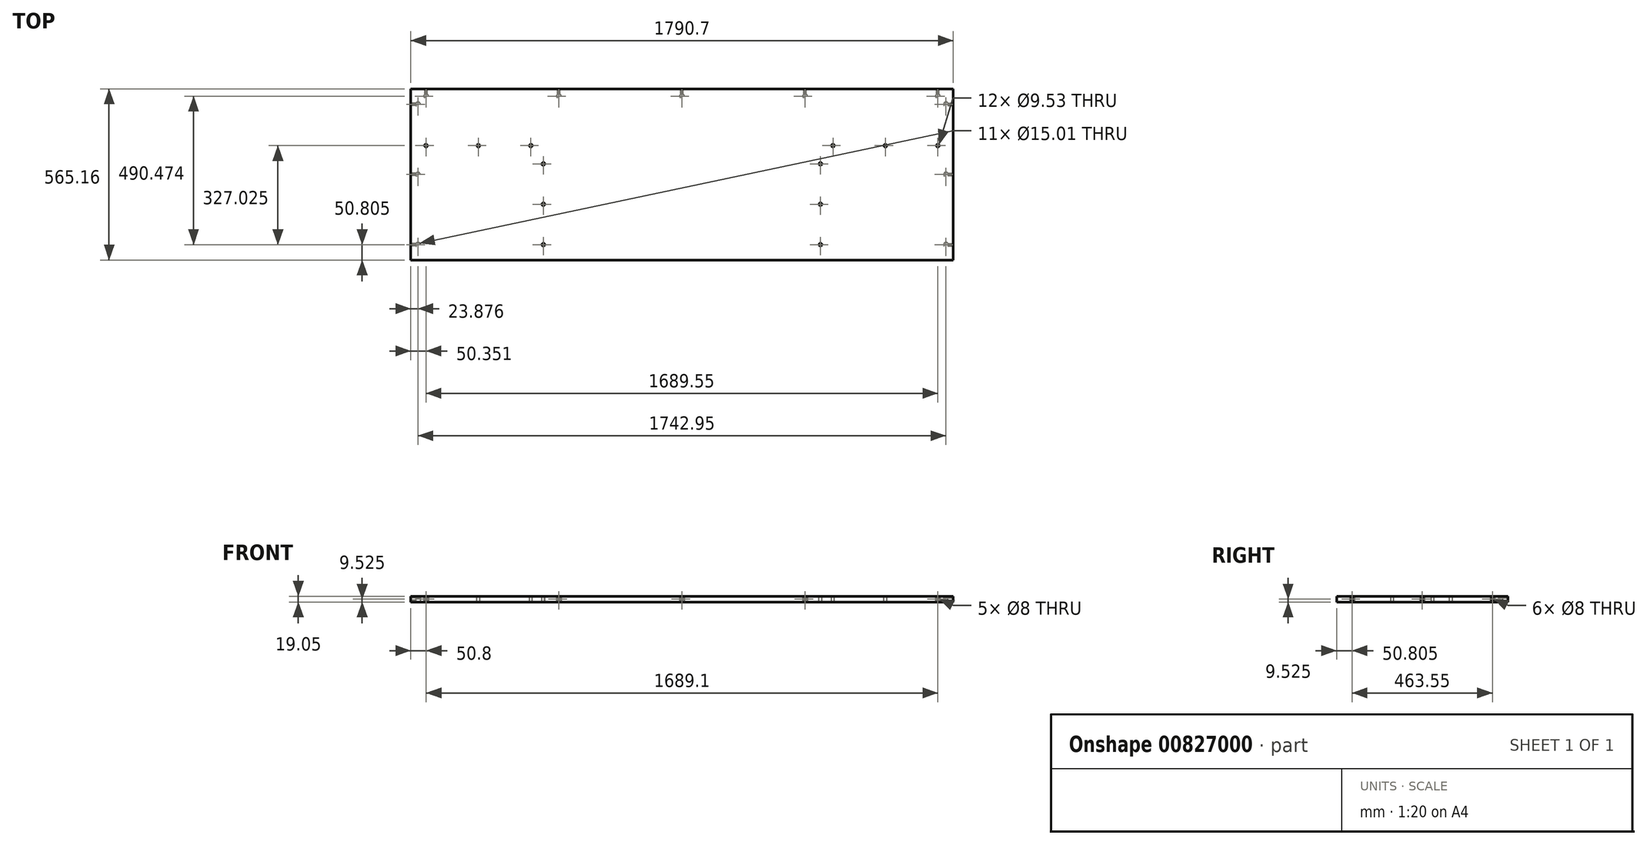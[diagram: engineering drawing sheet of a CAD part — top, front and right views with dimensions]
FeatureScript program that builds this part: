
annotation { "Feature Type Name" : "Feature", "Feature Type Description" : "" }
export const myFeature = defineFeature(function(context is Context, id is Id, definition is map)
    precondition{}
    {
        {
            var Q0;
            Q0=qCreatedBy(makeId("Top.planeOp"),FACE);
            var sketch = newSketch(context, id + "F0", { "sketchPlane" : qUnion([Q0])});
            skLineSegment(sketch, "E0.bottom", {"start": v(895.35, 282.58) * mm, "end": v(-895.35, 282.58) * mm});
            skLineSegment(sketch, "E0.top", {"start": v(895.35, -282.57) * mm, "end": v(-895.35, -282.57) * mm});
            skLineSegment(sketch, "E0.left", {"start": v(895.35, 282.58) * mm, "end": v(895.35, -282.57) * mm});
            skLineSegment(sketch, "E0.right", {"start": v(-895.35, 282.58) * mm, "end": v(-895.35, -282.57) * mm});
            skPoint(sketch, "E0.middle", {"position": v(0, 0) * mm});
            skSolve(sketch);
        }
        {
            var Q0;
            Q0=makeQuery(id+"F0.imprint","IMPRINT",FACE,{"disambiguationData":[TD([[makeQuery(id+"F0.imprint","IMPRINT",EDGE,{"derivedFrom":sQuery(id+"F0.wireOp",EDGE,"E0.bottom")}),1.0]])]});
            extrude(context, id + "F1", {"entities" : qUnion([Q0]), "depth" : 19.05 * mm, "offsetDistance" : 25.4 * mm});
        }
        {
            var Q0;
            Q0=makeQuery(id+"F1.opExtrude","CAP_FACE",FACE,{"disambiguationData":[OSD([sQuery(id+"F0.wireOp",EDGE,"E0.bottom"),sQuery(id+"F0.wireOp",EDGE,"E0.top"),sQuery(id+"F0.wireOp",EDGE,"E0.left"),sQuery(id+"F0.wireOp",EDGE,"E0.right")])],"isStart":false});
            var sketch = newSketch(context, id + "F2", { "sketchPlane" : qUnion([Q0])});
            skLineSegment(sketch, "E1.bottom", {"start": v(-895.35, 282.58) * mm, "end": v(-914.4, 282.58) * mm});
            skLineSegment(sketch, "E1.top", {"start": v(-895.35, -282.57) * mm, "end": v(-914.4, -282.57) * mm});
            skLineSegment(sketch, "E1.left", {"start": v(-895.35, 282.58) * mm, "end": v(-895.35, -282.57) * mm});
            skLineSegment(sketch, "E1.right", {"start": v(-914.4, 282.58) * mm, "end": v(-914.4, -282.57) * mm});
            skLineSegment(sketch, "E2.bottom", {"start": v(895.35, 282.58) * mm, "end": v(914.4, 282.58) * mm});
            skLineSegment(sketch, "E2.top", {"start": v(895.35, -282.57) * mm, "end": v(914.4, -282.57) * mm});
            skLineSegment(sketch, "E2.left", {"start": v(895.35, 282.58) * mm, "end": v(895.35, -282.57) * mm});
            skLineSegment(sketch, "E2.right", {"start": v(914.4, 282.58) * mm, "end": v(914.4, -282.57) * mm});
            skLineSegment(sketch, "E3", {"start": v(-914.4, -282.57) * mm, "end": v(-913.26, -282.57) * mm});
            skLineSegment(sketch, "E4.bottom", {"start": v(-913.26, -282.57) * mm, "end": v(-459.1, -282.57) * mm});
            skLineSegment(sketch, "E4.top", {"start": v(-913.26, -301.62) * mm, "end": v(-459.1, -301.62) * mm});
            skLineSegment(sketch, "E4.left", {"start": v(-913.26, -282.57) * mm, "end": v(-913.26, -301.62) * mm});
            skLineSegment(sketch, "E4.right", {"start": v(-459.1, -282.57) * mm, "end": v(-459.1, -301.62) * mm});
            skLineSegment(sketch, "E5", {"start": v(-459.1, -282.57) * mm, "end": v(-455.93, -282.57) * mm});
            skLineSegment(sketch, "E6.bottom", {"start": v(-455.93, -282.57) * mm, "end": v(-1.78, -282.57) * mm});
            skLineSegment(sketch, "E6.top", {"start": v(-455.93, -301.62) * mm, "end": v(-1.78, -301.62) * mm});
            skLineSegment(sketch, "E6.left", {"start": v(-455.93, -282.57) * mm, "end": v(-455.93, -301.62) * mm});
            skLineSegment(sketch, "E6.right", {"start": v(-1.78, -282.57) * mm, "end": v(-1.78, -301.62) * mm});
            skLineSegment(sketch, "E7", {"start": v(-1.78, -282.57) * mm, "end": v(1.4, -282.57) * mm});
            skLineSegment(sketch, "E8.bottom", {"start": v(1.4, -282.57) * mm, "end": v(455.55, -282.57) * mm});
            skLineSegment(sketch, "E8.top", {"start": v(1.4, -301.62) * mm, "end": v(455.55, -301.62) * mm});
            skLineSegment(sketch, "E8.left", {"start": v(1.4, -282.57) * mm, "end": v(1.4, -301.62) * mm});
            skLineSegment(sketch, "E8.right", {"start": v(455.55, -282.57) * mm, "end": v(455.55, -301.62) * mm});
            skLineSegment(sketch, "E9", {"start": v(455.55, -282.57) * mm, "end": v(458.72, -282.57) * mm});
            skLineSegment(sketch, "E10.bottom", {"start": v(458.72, -282.57) * mm, "end": v(912.88, -282.57) * mm});
            skLineSegment(sketch, "E10.top", {"start": v(458.72, -301.62) * mm, "end": v(912.88, -301.62) * mm});
            skLineSegment(sketch, "E10.left", {"start": v(458.72, -282.57) * mm, "end": v(458.72, -301.62) * mm});
            skLineSegment(sketch, "E10.right", {"start": v(912.88, -282.57) * mm, "end": v(912.88, -301.62) * mm});
            skLineSegment(sketch, "E11.left", {"start": v(-895.35, 282.58) * mm, "end": v(-895.8, 104.78) * mm});
            skLineSegment(sketch, "E11.right", {"start": v(895.8, 282.57) * mm, "end": v(895.35, 104.78) * mm});
            skLineSegment(sketch, "E12.left", {"start": v(-895.8, 104.78) * mm, "end": v(-895.8, 85.73) * mm});
            skLineSegment(sketch, "E12.right", {"start": v(895.35, 104.78) * mm, "end": v(895.35, 85.73) * mm});
            skLineSegment(sketch, "E13", {"start": v(-895.8, 95.25) * mm, "end": v(-845, 95.25) * mm});
            skLineSegment(sketch, "E14", {"start": v(895.35, 95.25) * mm, "end": v(844.55, 95.25) * mm});
            skLineSegment(sketch, "E15", {"start": v(-457.52, -282.57) * mm, "end": v(-457.68, 85.72) * mm});
            skLineSegment(sketch, "E16", {"start": v(457.14, -282.57) * mm, "end": v(457.14, 85.73) * mm});
            skLineSegment(sketch, "E17", {"start": v(-457.68, 85.72) * mm, "end": v(-457.66, 34.93) * mm});
            skLineSegment(sketch, "E18", {"start": v(-457.52, -282.57) * mm, "end": v(-457.54, -231.78) * mm});
            skLineSegment(sketch, "E19", {"start": v(457.14, -282.57) * mm, "end": v(457.14, -231.77) * mm});
            skLineSegment(sketch, "E20", {"start": v(457.14, 85.73) * mm, "end": v(457.14, 34.93) * mm});
            skPoint(sketch, "E21", {"position": v(-457.6, -98.43) * mm});
            skPoint(sketch, "E22", {"position": v(-457.66, 34.93) * mm});
            skPoint(sketch, "E23", {"position": v(-457.54, -231.78) * mm});
            skPoint(sketch, "E24", {"position": v(457.14, -231.77) * mm});
            skPoint(sketch, "E25", {"position": v(457.14, 34.93) * mm});
            skPoint(sketch, "E26", {"position": v(457.14, -98.42) * mm});
            skLineSegment(sketch, "E27.bottom", {"start": v(-448.07, 85.73) * mm, "end": v(-467.12, 85.73) * mm});
            skLineSegment(sketch, "E27.top", {"start": v(-448.07, -282.57) * mm, "end": v(-467.12, -282.57) * mm});
            skLineSegment(sketch, "E27.left", {"start": v(-448.07, 85.72) * mm, "end": v(-448.07, -282.58) * mm});
            skLineSegment(sketch, "E27.right", {"start": v(-467.12, 85.72) * mm, "end": v(-467.12, -282.58) * mm});
            skLineSegment(sketch, "E28.bottom", {"start": v(466.66, 85.73) * mm, "end": v(447.61, 85.73) * mm});
            skLineSegment(sketch, "E28.top", {"start": v(466.66, -282.57) * mm, "end": v(447.61, -282.57) * mm});
            skLineSegment(sketch, "E28.left", {"start": v(466.66, 85.73) * mm, "end": v(466.66, -282.57) * mm});
            skLineSegment(sketch, "E28.right", {"start": v(447.61, 85.73) * mm, "end": v(447.61, -282.57) * mm});
            skLineSegment(sketch, "E29.bottom", {"start": v(-448.07, 85.73) * mm, "end": v(-895.8, 85.73) * mm});
            skLineSegment(sketch, "E29.top", {"start": v(-448.07, 104.78) * mm, "end": v(-895.8, 104.78) * mm});
            skLineSegment(sketch, "E29.left", {"start": v(-448.07, 85.72) * mm, "end": v(-448.07, 104.78) * mm});
            skLineSegment(sketch, "E29.right", {"start": v(-895.8, 85.73) * mm, "end": v(-895.8, 104.78) * mm});
            skLineSegment(sketch, "E30.bottom", {"start": v(447.61, 85.73) * mm, "end": v(895.35, 85.73) * mm});
            skLineSegment(sketch, "E30.top", {"start": v(447.61, 104.78) * mm, "end": v(895.35, 104.78) * mm});
            skLineSegment(sketch, "E30.left", {"start": v(447.61, 85.73) * mm, "end": v(447.61, 104.78) * mm});
            skLineSegment(sketch, "E30.right", {"start": v(895.35, 85.73) * mm, "end": v(895.35, 104.78) * mm});
            skLineSegment(sketch, "E31", {"start": v(-448.07, 95.25) * mm, "end": v(-498.87, 95.25) * mm});
            skLineSegment(sketch, "E32", {"start": v(447.61, 95.25) * mm, "end": v(498.41, 95.25) * mm});
            skPoint(sketch, "E33", {"position": v(-671.94, 95.25) * mm});
            skPoint(sketch, "E34", {"position": v(-498.87, 95.25) * mm});
            skPoint(sketch, "E35", {"position": v(-845, 95.25) * mm});
            skPoint(sketch, "E36", {"position": v(498.41, 95.25) * mm});
            skPoint(sketch, "E37", {"position": v(844.55, 95.25) * mm});
            skLineSegment(sketch, "E38", {"start": v(671.48, 85.73) * mm, "end": v(671.48, 104.78) * mm});
            skPoint(sketch, "E39", {"position": v(671.48, 95.25) * mm});
            skPoint(sketch, "E40", {"position": v(-457.6, 85.72) * mm});
            skLineSegment(sketch, "E41", {"start": v(-671.94, 85.73) * mm, "end": v(-671.94, 104.78) * mm});
            skSolve(sketch);
        }
        {
            var Q0;
            Q0=sQuery(id+"F2.wireOp",VERTEX,"E35");
            var Q1;
            Q1=sQuery(id+"F2.wireOp",VERTEX,"E33");
            var Q2;
            Q2=sQuery(id+"F2.wireOp",VERTEX,"E34");
            var Q3;
            Q3=sQuery(id+"F2.wireOp",VERTEX,"E22");
            var Q4;
            Q4=sQuery(id+"F2.wireOp",VERTEX,"E21");
            var Q5;
            Q5=sQuery(id+"F2.wireOp",VERTEX,"E23");
            var Q6;
            Q6=sQuery(id+"F2.wireOp",VERTEX,"E24");
            var Q7;
            Q7=sQuery(id+"F2.wireOp",VERTEX,"E26");
            var Q8;
            Q8=sQuery(id+"F2.wireOp",VERTEX,"E25");
            var Q9;
            Q9=sQuery(id+"F2.wireOp",VERTEX,"E36");
            var Q10;
            Q10=sQuery(id+"F2.wireOp",VERTEX,"E39");
            var Q11;
            Q11=sQuery(id+"F2.wireOp",VERTEX,"E37");
            var Q12;
            Q12=makeQuery(id+"F1.opExtrude","SWEPT_BODY",BODY,{"disambiguationData":[OSD([sQuery(id+"F0.wireOp",EDGE,"E0.bottom"),sQuery(id+"F0.wireOp",EDGE,"E0.top"),sQuery(id+"F0.wireOp",EDGE,"E0.left"),sQuery(id+"F0.wireOp",EDGE,"E0.right")])]});
            hole(context, id + "F3", {"style" : HoleStyle.SIMPLE, "endStyle" : HoleEndStyle.BLIND, "holeDiameter" : 9.52 * mm, "majorDiameter" : 6.35 * mm, "holeDepth" : 25.4 * mm, "isTappedThrough" : true, "tappedDepth" : 12.7 * mm, "tapClearance" : 3, "startFromSketch" : true, "locations" : qUnion([Q0, Q1, Q2, Q3, Q4, Q5, Q6, Q7, Q8, Q9, Q10, Q11]), "scope" : qUnion([Q12])});
        }
        {
            var Q0;
            Q0=makeQuery(id+"F1.opExtrude","CAP_FACE",FACE,{"disambiguationData":[OSD([sQuery(id+"F0.wireOp",EDGE,"E0.bottom"),sQuery(id+"F0.wireOp",EDGE,"E0.top"),sQuery(id+"F0.wireOp",EDGE,"E0.left"),sQuery(id+"F0.wireOp",EDGE,"E0.right")])],"isStart":true});
            var sketch = newSketch(context, id + "F4", { "sketchPlane" : qUnion([Q0])});
            skLineSegment(sketch, "E42", {"start": v(-895.35, 282.57) * mm, "end": v(-871.47, 282.57) * mm});
            skLineSegment(sketch, "E43", {"start": v(-871.47, 282.57) * mm, "end": v(-871.47, 231.77) * mm});
            skLineSegment(sketch, "E44", {"start": v(-895.35, -282.58) * mm, "end": v(-871.47, -282.58) * mm});
            skLineSegment(sketch, "E45", {"start": v(-871.47, -282.58) * mm, "end": v(-871.47, -231.78) * mm});
            skLineSegment(sketch, "E46", {"start": v(-895.35, 0) * mm, "end": v(-871.47, 0) * mm});
            skLineSegment(sketch, "E47", {"start": v(895.35, 282.57) * mm, "end": v(871.47, 282.57) * mm});
            skLineSegment(sketch, "E48", {"start": v(871.47, 282.57) * mm, "end": v(871.47, 231.77) * mm});
            skLineSegment(sketch, "E49", {"start": v(895.35, -282.58) * mm, "end": v(871.47, -282.58) * mm});
            skLineSegment(sketch, "E50", {"start": v(871.47, -282.58) * mm, "end": v(871.47, -231.78) * mm});
            skLineSegment(sketch, "E51", {"start": v(895.35, 0) * mm, "end": v(871.47, 0) * mm});
            skPoint(sketch, "E52", {"position": v(-871.47, 231.77) * mm});
            skPoint(sketch, "E53", {"position": v(-871.47, 0) * mm});
            skPoint(sketch, "E54", {"position": v(-871.47, -231.78) * mm});
            skPoint(sketch, "E55", {"position": v(871.47, 231.77) * mm});
            skPoint(sketch, "E56", {"position": v(871.47, 0) * mm});
            skPoint(sketch, "E57", {"position": v(871.47, -231.78) * mm});
            skLineSegment(sketch, "E58", {"start": v(-895.35, -282.58) * mm, "end": v(-844.55, -282.58) * mm});
            skLineSegment(sketch, "E59", {"start": v(-844.55, -282.58) * mm, "end": v(-844.55, -258.7) * mm});
            skLineSegment(sketch, "E60", {"start": v(895.35, -282.58) * mm, "end": v(844.55, -282.58) * mm});
            skLineSegment(sketch, "E61", {"start": v(844.55, -282.58) * mm, "end": v(844.55, -258.7) * mm});
            skLineSegment(sketch, "E62", {"start": v(0, -282.58) * mm, "end": v(406.4, -282.58) * mm});
            skLineSegment(sketch, "E63", {"start": v(0, -282.58) * mm, "end": v(-406.4, -282.58) * mm});
            skLineSegment(sketch, "E64", {"start": v(0, -282.58) * mm, "end": v(0, -258.7) * mm});
            skLineSegment(sketch, "E65", {"start": v(-406.4, -282.58) * mm, "end": v(-406.4, -258.7) * mm});
            skLineSegment(sketch, "E66", {"start": v(406.4, -282.58) * mm, "end": v(406.4, -258.7) * mm});
            skPoint(sketch, "E67", {"position": v(-844.55, -258.7) * mm});
            skPoint(sketch, "E68", {"position": v(-406.4, -258.7) * mm});
            skPoint(sketch, "E69", {"position": v(0, -258.7) * mm});
            skPoint(sketch, "E70", {"position": v(406.4, -258.7) * mm});
            skPoint(sketch, "E71", {"position": v(844.55, -258.7) * mm});
            skSolve(sketch);
        }
        {
            var Q0;
            Q0=sQuery(id+"F4.wireOp",VERTEX,"E52");
            var Q1;
            Q1=sQuery(id+"F4.wireOp",VERTEX,"E53");
            var Q2;
            Q2=sQuery(id+"F4.wireOp",VERTEX,"E54");
            var Q3;
            Q3=sQuery(id+"F4.wireOp",VERTEX,"E67");
            var Q4;
            Q4=sQuery(id+"F4.wireOp",VERTEX,"E68");
            var Q5;
            Q5=sQuery(id+"F4.wireOp",VERTEX,"E69");
            var Q6;
            Q6=sQuery(id+"F4.wireOp",VERTEX,"E70");
            var Q7;
            Q7=sQuery(id+"F4.wireOp",VERTEX,"E71");
            var Q8;
            Q8=sQuery(id+"F4.wireOp",VERTEX,"E57");
            var Q9;
            Q9=sQuery(id+"F4.wireOp",VERTEX,"E56");
            var Q10;
            Q10=sQuery(id+"F4.wireOp",VERTEX,"E55");
            var Q11;
            Q11=makeQuery(id+"F1.opExtrude","SWEPT_BODY",BODY,{"disambiguationData":[OSD([sQuery(id+"F0.wireOp",EDGE,"E0.bottom"),sQuery(id+"F0.wireOp",EDGE,"E0.top"),sQuery(id+"F0.wireOp",EDGE,"E0.left"),sQuery(id+"F0.wireOp",EDGE,"E0.right")])]});
            hole(context, id + "F5", {"style" : HoleStyle.SIMPLE, "endStyle" : HoleEndStyle.BLIND, "holeDiameter" : 15 * mm, "majorDiameter" : 6.35 * mm, "holeDepth" : 14.22 * mm, "isTappedThrough" : true, "tappedDepth" : 12.7 * mm, "tapClearance" : 3, "startFromSketch" : true, "locations" : qUnion([Q0, Q1, Q2, Q3, Q4, Q5, Q6, Q7, Q8, Q9, Q10]), "scope" : qUnion([Q11])});
        }
        {
            var Q0;
            Q0=makeQuery(id+"F1.opExtrude","SWEPT_FACE",FACE,{"disambiguationData":[OSD([sQuery(id+"F0.wireOp",EDGE,"E0.bottom")])]});
            var sketch = newSketch(context, id + "F6", { "sketchPlane" : qUnion([Q0])});
            skLineSegment(sketch, "E72", {"start": v(-895.35, 9.53) * mm, "end": v(-844.55, 9.53) * mm});
            skLineSegment(sketch, "E73", {"start": v(895.35, 9.53) * mm, "end": v(844.55, 9.53) * mm});
            skLineSegment(sketch, "E74", {"start": v(0, 0) * mm, "end": v(0, 19.05) * mm});
            skPoint(sketch, "E75", {"position": v(0, 9.53) * mm});
            skLineSegment(sketch, "E76", {"start": v(0, 9.53) * mm, "end": v(406.4, 9.53) * mm});
            skLineSegment(sketch, "E77", {"start": v(0, 9.53) * mm, "end": v(-406.4, 9.53) * mm});
            skPoint(sketch, "E78", {"position": v(-844.55, 9.53) * mm});
            skPoint(sketch, "E79", {"position": v(-406.4, 9.53) * mm});
            skPoint(sketch, "E80", {"position": v(406.4, 9.53) * mm});
            skPoint(sketch, "E81", {"position": v(844.55, 9.53) * mm});
            skSolve(sketch);
        }
        {
            var Q0;
            Q0=sQuery(id+"F6.wireOp",VERTEX,"E78");
            var Q1;
            Q1=sQuery(id+"F6.wireOp",VERTEX,"E79");
            var Q2;
            Q2=sQuery(id+"F6.wireOp",VERTEX,"E75");
            var Q3;
            Q3=sQuery(id+"F6.wireOp",VERTEX,"E80");
            var Q4;
            Q4=sQuery(id+"F6.wireOp",VERTEX,"E81");
            var Q5;
            Q5=makeQuery(id+"F1.opExtrude","SWEPT_BODY",BODY,{"disambiguationData":[OSD([sQuery(id+"F0.wireOp",EDGE,"E0.bottom"),sQuery(id+"F0.wireOp",EDGE,"E0.top"),sQuery(id+"F0.wireOp",EDGE,"E0.left"),sQuery(id+"F0.wireOp",EDGE,"E0.right")])]});
            hole(context, id + "F7", {"style" : HoleStyle.SIMPLE, "endStyle" : HoleEndStyle.BLIND, "holeDiameter" : 8 * mm, "majorDiameter" : 6.35 * mm, "holeDepth" : 25.4 * mm, "isTappedThrough" : true, "tappedDepth" : 12.7 * mm, "tapClearance" : 3, "startFromSketch" : true, "locations" : qUnion([Q0, Q1, Q2, Q3, Q4]), "scope" : qUnion([Q5])});
        }
        {
            var Q0;
            Q0=makeQuery(id+"F1.opExtrude","SWEPT_FACE",FACE,{"disambiguationData":[OSD([sQuery(id+"F0.wireOp",EDGE,"E0.right")])]});
            var sketch = newSketch(context, id + "F8", { "sketchPlane" : qUnion([Q0])});
            skLineSegment(sketch, "E82", {"start": v(-282.58, 9.53) * mm, "end": v(-231.78, 9.53) * mm});
            skLineSegment(sketch, "E83", {"start": v(282.57, 9.53) * mm, "end": v(231.77, 9.53) * mm});
            skLineSegment(sketch, "E84", {"start": v(0, 0) * mm, "end": v(0, 19.05) * mm});
            skPoint(sketch, "E85", {"position": v(-231.78, 9.53) * mm});
            skPoint(sketch, "E86", {"position": v(0, 9.53) * mm});
            skPoint(sketch, "E87", {"position": v(231.77, 9.53) * mm});
            skSolve(sketch);
        }
        {
            var Q0;
            Q0=sQuery(id+"F8.wireOp",VERTEX,"E85");
            var Q1;
            Q1=sQuery(id+"F8.wireOp",VERTEX,"E86");
            var Q2;
            Q2=sQuery(id+"F8.wireOp",VERTEX,"E87");
            var Q3;
            Q3=makeQuery(id+"F1.opExtrude","SWEPT_BODY",BODY,{"disambiguationData":[OSD([sQuery(id+"F0.wireOp",EDGE,"E0.bottom"),sQuery(id+"F0.wireOp",EDGE,"E0.top"),sQuery(id+"F0.wireOp",EDGE,"E0.left"),sQuery(id+"F0.wireOp",EDGE,"E0.right")])]});
            hole(context, id + "F9", {"style" : HoleStyle.SIMPLE, "endStyle" : HoleEndStyle.BLIND, "holeDiameter" : 8 * mm, "majorDiameter" : 6.35 * mm, "holeDepth" : 25.4 * mm, "isTappedThrough" : true, "tappedDepth" : 12.7 * mm, "tapClearance" : 3, "startFromSketch" : true, "locations" : qUnion([Q0, Q1, Q2]), "scope" : qUnion([Q3])});
        }
        {
            var Q0;
            Q0=makeQuery(id+"F1.opExtrude","SWEPT_FACE",FACE,{"disambiguationData":[OSD([sQuery(id+"F0.wireOp",EDGE,"E0.left")])]});
            var sketch = newSketch(context, id + "F10", { "sketchPlane" : qUnion([Q0])});
            skLineSegment(sketch, "E88", {"start": v(-282.57, 9.53) * mm, "end": v(-231.77, 9.53) * mm});
            skLineSegment(sketch, "E89", {"start": v(282.58, 9.53) * mm, "end": v(231.78, 9.53) * mm});
            skLineSegment(sketch, "E90", {"start": v(0, 19.05) * mm, "end": v(0, 0) * mm});
            skPoint(sketch, "E91", {"position": v(0, 9.53) * mm});
            skPoint(sketch, "E92", {"position": v(231.78, 9.53) * mm});
            skPoint(sketch, "E93", {"position": v(-231.77, 9.53) * mm});
            skSolve(sketch);
        }
        {
            var Q0;
            Q0=sQuery(id+"F10.wireOp",VERTEX,"E93");
            var Q1;
            Q1=sQuery(id+"F10.wireOp",VERTEX,"E91");
            var Q2;
            Q2=sQuery(id+"F10.wireOp",VERTEX,"E92");
            var Q3;
            Q3=makeQuery(id+"F1.opExtrude","SWEPT_BODY",BODY,{"disambiguationData":[OSD([sQuery(id+"F0.wireOp",EDGE,"E0.bottom"),sQuery(id+"F0.wireOp",EDGE,"E0.top"),sQuery(id+"F0.wireOp",EDGE,"E0.left"),sQuery(id+"F0.wireOp",EDGE,"E0.right")])]});
            hole(context, id + "F11", {"style" : HoleStyle.SIMPLE, "endStyle" : HoleEndStyle.BLIND, "holeDiameter" : 8 * mm, "majorDiameter" : 6.35 * mm, "holeDepth" : 25.4 * mm, "isTappedThrough" : true, "tappedDepth" : 12.7 * mm, "tapClearance" : 3, "startFromSketch" : true, "locations" : qUnion([Q0, Q1, Q2]), "scope" : qUnion([Q3])});
        }
    });
